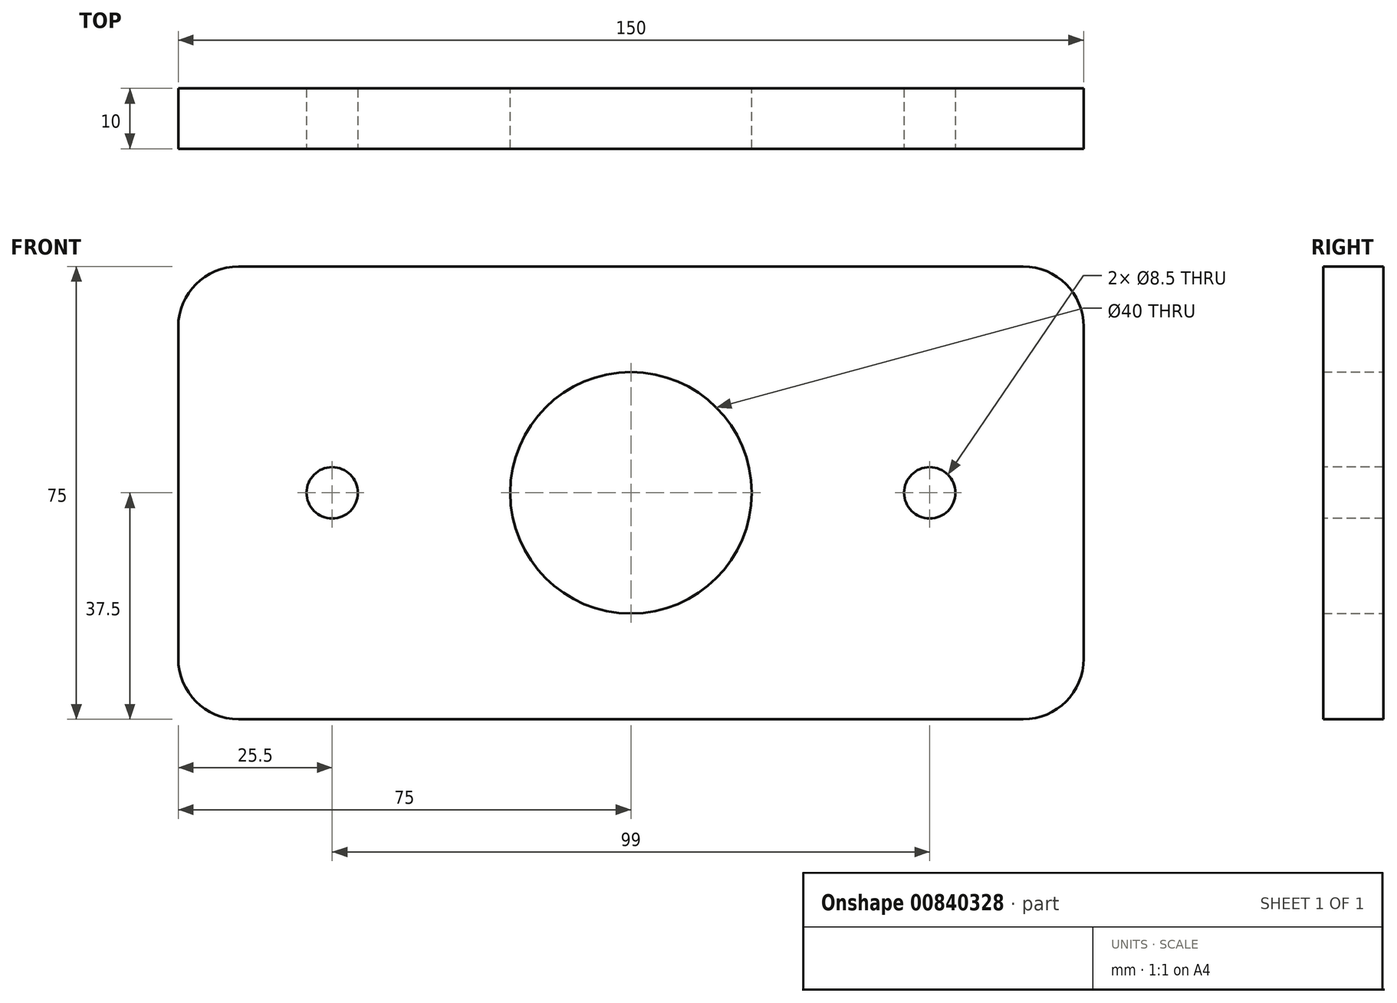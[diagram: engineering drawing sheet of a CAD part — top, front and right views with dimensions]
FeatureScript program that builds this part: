
annotation { "Feature Type Name" : "Feature", "Feature Type Description" : "" }
export const myFeature = defineFeature(function(context is Context, id is Id, definition is map)
    precondition{}
    {
        {
            var Q0;
            Q0=qCreatedBy(makeId("Front.planeOp"),FACE);
            var sketch = newSketch(context, id + "F0", { "sketchPlane" : qUnion([Q0])});
            skLineSegment(sketch, "E0.bottom", {"start": v(-75, 37.5) * mm, "end": v(75, 37.5) * mm});
            skLineSegment(sketch, "E0.top", {"start": v(-75, -37.5) * mm, "end": v(75, -37.5) * mm});
            skLineSegment(sketch, "E0.left", {"start": v(-75, 37.5) * mm, "end": v(-75, -37.5) * mm});
            skLineSegment(sketch, "E0.right", {"start": v(75, 37.5) * mm, "end": v(75, -37.5) * mm});
            skPoint(sketch, "E0.middle", {"position": v(0, 0) * mm});
            skCircle(sketch, "E1", {"center": v(0, 0) * mm, "radius": 20 * mm});
            skSolve(sketch);
        }
        {
            var Q0;
            Q0 = qSketchRegion(id + "F0", true);
            extrude(context, id + "F1", {"entities" : qUnion([Q0]), "endBound" : BoundingType.SYMMETRIC, "depth" : 10 * mm, "offsetDistance" : 25 * mm});
        }
        {
            var Q0;
            Q0=makeQuery(id+"F1.opExtrude","SWEPT_EDGE",EDGE,{"disambiguationData":[OSD([sQuery(id+"F0.wireOp",EDGE,"E0.bottom"),sQuery(id+"F0.wireOp",EDGE,"E0.left")])]});
            var Q1;
            Q1=makeQuery(id+"F1.opExtrude","SWEPT_EDGE",EDGE,{"disambiguationData":[OSD([sQuery(id+"F0.wireOp",EDGE,"E0.bottom"),sQuery(id+"F0.wireOp",EDGE,"E0.right")])]});
            var Q2;
            Q2=makeQuery(id+"F1.opExtrude","SWEPT_EDGE",EDGE,{"disambiguationData":[OSD([sQuery(id+"F0.wireOp",EDGE,"E0.top"),sQuery(id+"F0.wireOp",EDGE,"E0.right")])]});
            var Q3;
            Q3=makeQuery(id+"F1.opExtrude","SWEPT_EDGE",EDGE,{"disambiguationData":[OSD([sQuery(id+"F0.wireOp",EDGE,"E0.top"),sQuery(id+"F0.wireOp",EDGE,"E0.left")])]});
            fillet(context, id + "F2", {"entities" : qUnion([Q0, Q1, Q2, Q3]), "radius" : 10 * mm, "tangentPropagation" : true, "allowEdgeOverflow" : false});
        }
        {
            var Q0;
            Q0=makeQuery(id+"F1.opExtrude","CAP_FACE",FACE,{"disambiguationData":[OSD([sQuery(id+"F0.wireOp",EDGE,"E0.bottom"),sQuery(id+"F0.wireOp",EDGE,"E0.top"),sQuery(id+"F0.wireOp",EDGE,"E0.left"),sQuery(id+"F0.wireOp",EDGE,"E0.right"),sQuery(id+"F0.wireOp",EDGE,"E1")])],"isStart":false});
            var sketch = newSketch(context, id + "F3", { "sketchPlane" : qUnion([Q0])});
            skPoint(sketch, "E2", {"position": v(-49.5, 0) * mm});
            skPoint(sketch, "E3", {"position": v(49.5, 0) * mm});
            skSolve(sketch);
        }
        {
            var Q0;
            Q0=sQuery(id+"F3.wireOp",VERTEX,"E2");
            var Q1;
            Q1=sQuery(id+"F3.wireOp",VERTEX,"E3");
            var Q2;
            Q2=makeQuery(id+"F1.opExtrude","SWEPT_BODY",BODY,{"disambiguationData":[OSD([sQuery(id+"F0.wireOp",EDGE,"E0.bottom"),sQuery(id+"F0.wireOp",EDGE,"E0.top"),sQuery(id+"F0.wireOp",EDGE,"E0.left"),sQuery(id+"F0.wireOp",EDGE,"E0.right"),sQuery(id+"F0.wireOp",EDGE,"E1")])]});
            hole(context, id + "F4", {"style" : HoleStyle.SIMPLE, "endStyle" : HoleEndStyle.BLIND, "standardTappedOrClearance" : lookupTablePath({ "standard" : "ISO", "engagement" : "75%", "pitch" : "1.5 mm", "size" : "M10", "type" : "Tapped" }), "standardBlindInLast" : lookupTablePath({ "standard" : "ISO", "engagement" : "75%", "pitch" : "1.5 mm", "size" : "M10", "type" : "Tapped" }), "holeDiameter" : 8.5 * mm, "majorDiameter" : 10 * mm, "showTappedDepth" : true, "holeDepth" : 24.5 * mm, "isTappedThrough" : true, "tappedDepth" : 20 * mm, "tapClearance" : 3, "startFromSketch" : true, "locations" : qUnion([Q0, Q1]), "scope" : qUnion([Q2])});
        }
    });
